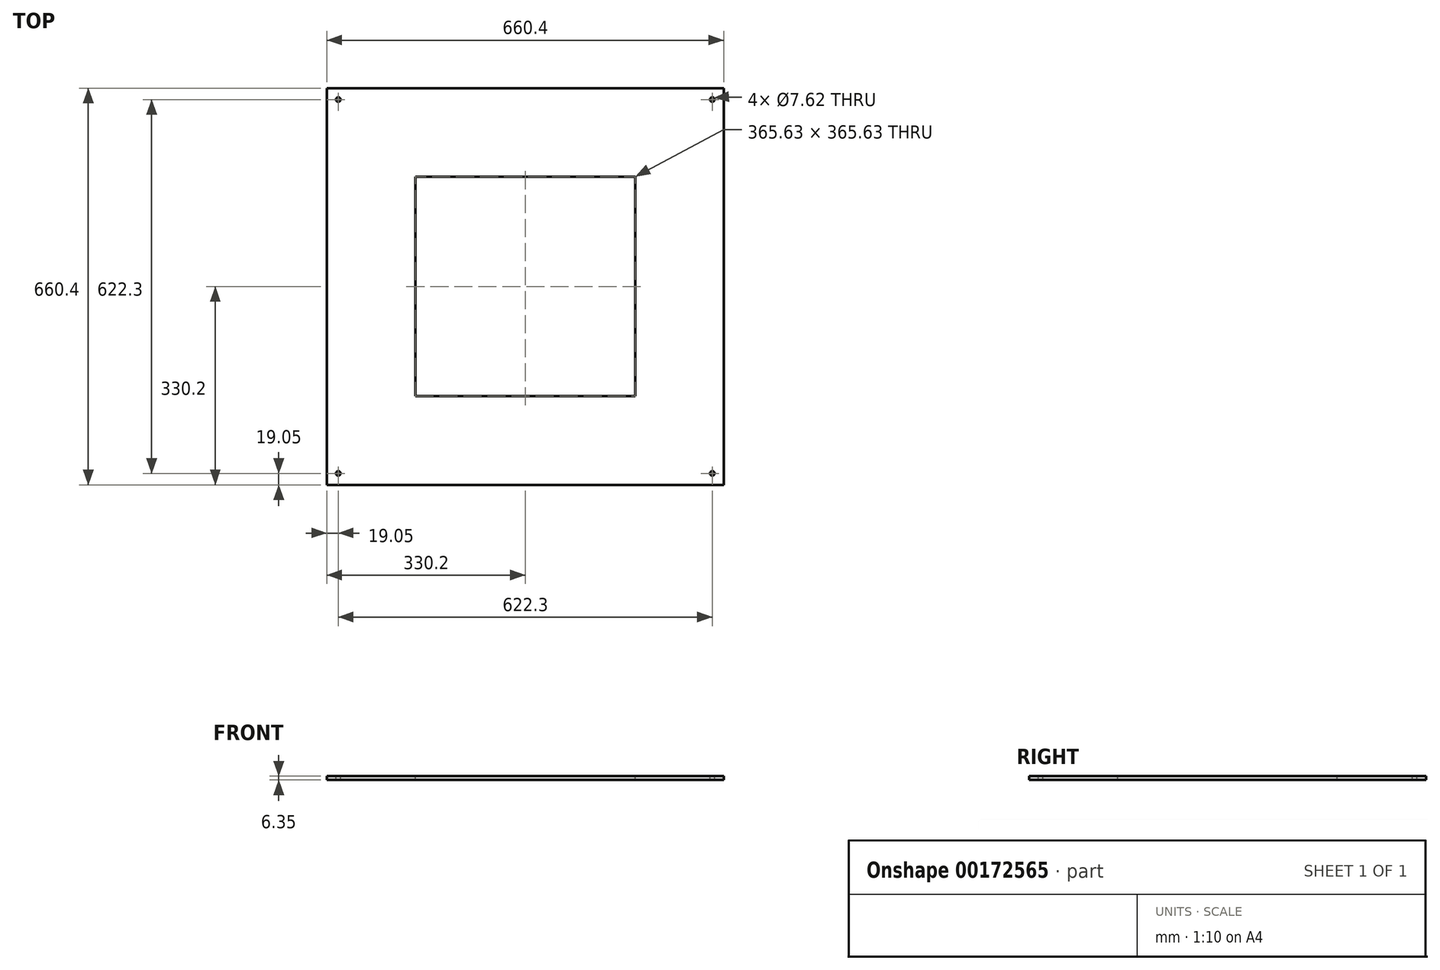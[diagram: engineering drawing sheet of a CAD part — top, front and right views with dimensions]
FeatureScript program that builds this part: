
annotation { "Feature Type Name" : "Feature", "Feature Type Description" : "" }
export const myFeature = defineFeature(function(context is Context, id is Id, definition is map)
    precondition{}
    {
        {
            var Q0;
            Q0=qCreatedBy(makeId("Top.planeOp"),FACE);
            var sketch = newSketch(context, id + "F0", { "sketchPlane" : qUnion([Q0])});
            skLineSegment(sketch, "E0.bottom", {"start": v(330.2, -330.2) * mm, "end": v(-330.2, -330.2) * mm});
            skLineSegment(sketch, "E0.top", {"start": v(330.2, 330.2) * mm, "end": v(-330.2, 330.2) * mm});
            skLineSegment(sketch, "E0.left", {"start": v(330.2, -330.2) * mm, "end": v(330.2, 330.2) * mm});
            skLineSegment(sketch, "E0.right", {"start": v(-330.2, -330.2) * mm, "end": v(-330.2, 330.2) * mm});
            skPoint(sketch, "E0.middle", {"position": v(0, 0) * mm});
            skCircle(sketch, "E1", {"center": v(0, 0) * mm, "radius": 96.84 * mm, "construction": true});
            skCircle(sketch, "E2", {"center": v(51.52, -141.54) * mm, "radius": 12.5 * mm, "construction": true});
            skCircle(sketch, "E3.1.0", {"center": v(-63.66, -136.5) * mm, "radius": 12.5 * mm, "construction": true});
            skCircle(sketch, "E3.2.0", {"center": v(-141.54, -51.52) * mm, "radius": 12.5 * mm, "construction": true});
            skCircle(sketch, "E3.3.0", {"center": v(-136.5, 63.66) * mm, "radius": 12.5 * mm, "construction": true});
            skCircle(sketch, "E3.4.0", {"center": v(-51.52, 141.54) * mm, "radius": 12.5 * mm, "construction": true});
            skLineSegment(sketch, "E3.anchor1", {"start": v(0, 0) * mm, "end": v(51.52, -141.54) * mm, "construction": true});
            skLineSegment(sketch, "E3.anchor2", {"start": v(0, 0) * mm, "end": v(-51.52, 141.54) * mm, "construction": true});
            skCircle(sketch, "E4", {"center": v(0, 0) * mm, "radius": 127 * mm});
            skCircle(sketch, "E5", {"center": v(51.52, -141.54) * mm, "radius": 28.58 * mm});
            skCircle(sketch, "E6", {"center": v(-63.66, -136.5) * mm, "radius": 28.58 * mm});
            skCircle(sketch, "E7", {"center": v(-51.52, 141.54) * mm, "radius": 28.58 * mm});
            skCircle(sketch, "E8", {"center": v(-136.5, 63.66) * mm, "radius": 28.58 * mm});
            skCircle(sketch, "E9", {"center": v(-141.54, -51.52) * mm, "radius": 28.58 * mm});
            skSolve(sketch);
        }
        {
            var Q0;
            Q0=makeQuery(id+"F0.imprint","IMPRINT",FACE,{"disambiguationData":[TD([[makeQuery(id+"F0.imprint","IMPRINT",EDGE,{"derivedFrom":sQuery(id+"F0.wireOp",EDGE,"E0.bottom")}),-1.0]])]});
            extrude(context, id + "F1", {"entities" : qUnion([Q0]), "depth" : 6.35 * mm});
        }
        {
            var Q0;
            Q0=makeQuery(id+"F1.opExtrude","CAP_FACE",FACE,{"disambiguationData":[OSD([sQuery(id+"F0.wireOp",EDGE,"E0.bottom"),sQuery(id+"F0.wireOp",EDGE,"E0.top"),sQuery(id+"F0.wireOp",EDGE,"E0.left"),sQuery(id+"F0.wireOp",EDGE,"E0.right"),sQuery(id+"F0.wireOp",EDGE,"E4"),sQuery(id+"F0.wireOp",EDGE,"E5"),sQuery(id+"F0.wireOp",EDGE,"E6"),sQuery(id+"F0.wireOp",EDGE,"E7"),sQuery(id+"F0.wireOp",EDGE,"E8"),sQuery(id+"F0.wireOp",EDGE,"E9")])],"isStart":false});
            var sketch = newSketch(context, id + "F2", { "sketchPlane" : qUnion([Q0])});
            skLineSegment(sketch, "E10.bottom", {"start": v(182.81, -182.81) * mm, "end": v(-182.81, -182.81) * mm});
            skLineSegment(sketch, "E10.top", {"start": v(182.81, 182.81) * mm, "end": v(-182.81, 182.81) * mm});
            skLineSegment(sketch, "E10.left", {"start": v(182.81, -182.81) * mm, "end": v(182.81, 182.81) * mm});
            skLineSegment(sketch, "E10.right", {"start": v(-182.81, -182.81) * mm, "end": v(-182.81, 182.81) * mm});
            skPoint(sketch, "E10.middle", {"position": v(0, 0) * mm});
            skLineSegment(sketch, "E11", {"start": v(-311.15, 330.2) * mm, "end": v(-311.15, 311.15) * mm, "construction": true});
            skLineSegment(sketch, "E12", {"start": v(-311.15, 311.15) * mm, "end": v(-330.2, 311.15) * mm, "construction": true});
            skCircle(sketch, "E13", {"center": v(-311.15, 311.15) * mm, "radius": 3.81 * mm});
            skCircle(sketch, "E14.0.1.0", {"center": v(-311.15, -311.15) * mm, "radius": 3.81 * mm});
            skCircle(sketch, "E14.1.0.0", {"center": v(311.15, 311.15) * mm, "radius": 3.81 * mm});
            skCircle(sketch, "E14.1.1.0", {"center": v(311.15, -311.15) * mm, "radius": 3.81 * mm});
            skLineSegment(sketch, "E14.direction1", {"start": v(-311.15, 311.15) * mm, "end": v(311.15, 311.15) * mm, "construction": true});
            skLineSegment(sketch, "E14.direction2", {"start": v(-311.15, 311.15) * mm, "end": v(-311.15, -311.15) * mm, "construction": true});
            skSolve(sketch);
        }
        {
            var Q0;
            Q0 = qSketchRegion(id + "F2", true);
            extrude(context, id + "F3", {"entities" : qUnion([Q0]), "operationType" : NewBodyOperationType.REMOVE, "oppositeDirection" : true, "depth" : 25.4 * mm});
        }
    });
